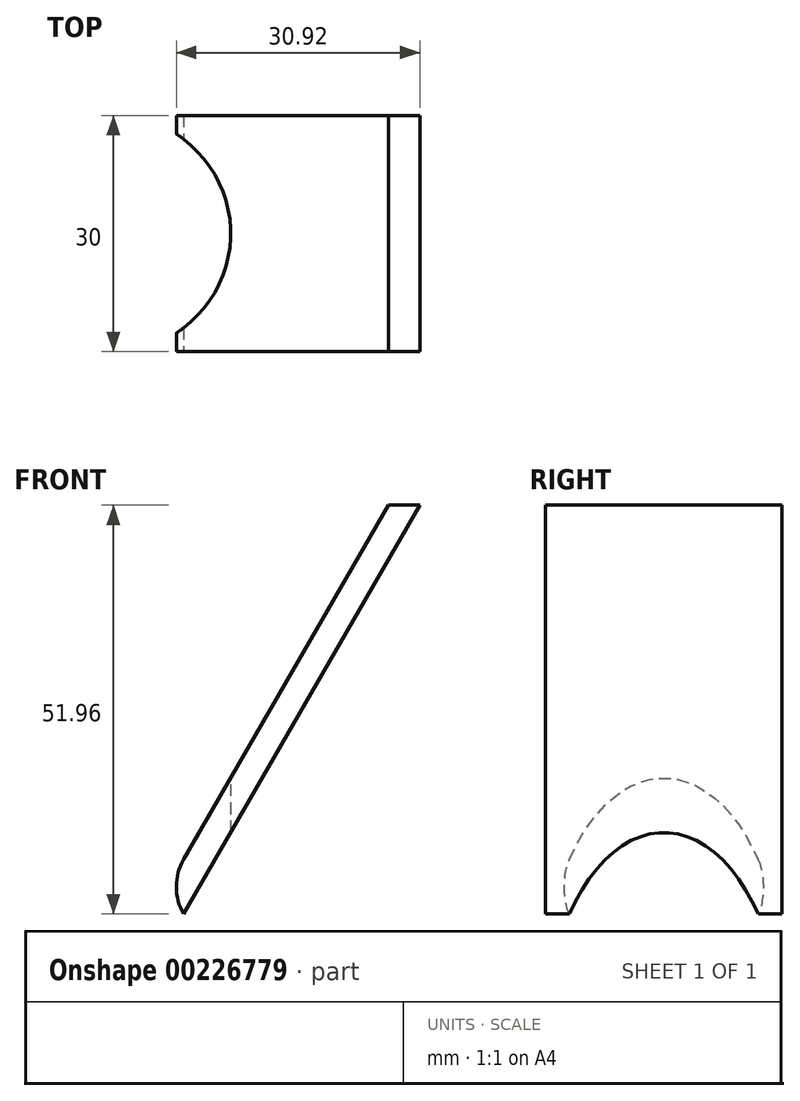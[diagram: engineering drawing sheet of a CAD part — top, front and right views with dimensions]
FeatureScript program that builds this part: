
annotation { "Feature Type Name" : "Feature", "Feature Type Description" : "" }
export const myFeature = defineFeature(function(context is Context, id is Id, definition is map)
    precondition{}
    {
        {
            var Q0;
            Q0=qCreatedBy(makeId("Top.planeOp"),FACE);
            var sketch = newSketch(context, id + "F0", { "sketchPlane" : qUnion([Q0])});
            skCircle(sketch, "E0", {"center": v(0, 0) * mm, "radius": 15 * mm});
            skCircle(sketch, "E1", {"center": v(0, 0) * mm, "radius": 12 * mm});
            skCircle(sketch, "E2", {"center": v(0, 0) * mm, "radius": 1.75 * mm});
            skSolve(sketch);
        }
        {
            var Q0;
            Q0=makeQuery(id+"F0.imprint","IMPRINT",FACE,{"disambiguationData":[TD([[makeQuery(id+"F0.imprint","IMPRINT",EDGE,{"derivedFrom":sQuery(id+"F0.wireOp",EDGE,"E0")}),1.0]])]});
            extrude(context, id + "F1", {"entities" : qUnion([Q0]), "oppositeDirection" : true, "depth" : 90 * mm});
        }
        {
            var Q0;
            Q0=makeQuery(id+"F0.imprint","IMPRINT",FACE,{"disambiguationData":[TD([[makeQuery(id+"F0.imprint","IMPRINT",EDGE,{"derivedFrom":sQuery(id+"F0.wireOp",EDGE,"E1")}),1.0]])]});
            extrude(context, id + "F2", {"entities" : qUnion([Q0]), "operationType" : NewBodyOperationType.ADD, "oppositeDirection" : true, "depth" : 8 * mm});
        }
        {
            var Q0;
            Q0=qCreatedBy(makeId("Right.planeOp"),FACE);
            cPlane(context, id + "F3", {"entities" : qUnion([Q0]), "cplaneType" : CPlaneType.OFFSET, "offset" : 15 * mm, "width" : 150 * mm, "height" : 150 * mm});
        }
        {
            var Q0;
            Q0=qCreatedBy(id+"F3.planeOp",FACE);
            var sketch = newSketch(context, id + "F4", { "sketchPlane" : qUnion([Q0])});
            skCircle(sketch, "E3", {"center": v(0, -25.75) * mm, "radius": 14.75 * mm});
            skLineSegment(sketch, "E4", {"start": v(12.69, -18.23) * mm, "end": v(12.69, -33.27) * mm});
            skLineSegment(sketch, "E5", {"start": v(-12.69, -18.23) * mm, "end": v(-12.69, -33.27) * mm});
            skLineSegment(sketch, "E6", {"start": v(-12.69, -18.23) * mm, "end": v(12.69, -18.23) * mm, "construction": true});
            skLineSegment(sketch, "E7", {"start": v(-12.69, -33.27) * mm, "end": v(12.69, -33.27) * mm, "construction": true});
            skLineSegment(sketch, "E8", {"start": v(-12.69, -25.75) * mm, "end": v(12.69, -25.75) * mm, "construction": true});
            skSolve(sketch);
        }
        {
            var Q0;
            {var subQ0=sQuery(id+"F4.wireOp",EDGE,"E4");Q0=makeQuery(id+"F4.imprint","IMPRINT",FACE,{"disambiguationData":[TD([[makeQuery(id+"F4.imprint","IMPRINT",EDGE,{"derivedFrom":subQ0}),-1.0]])]});}
            extrude(context, id + "F5", {"entities" : qUnion([Q0]), "operationType" : NewBodyOperationType.REMOVE, "oppositeDirection" : true, "depth" : 11.6 * mm});
        }
        {
            var Q0;
            Q0=makeQuery(id+"F5.boolean.opBoolean","INTERSECT",EDGE,{"disambiguationData":[OD(1.0)],"derivedFrom":[makeQuery(id+"F1.opExtrude","SWEPT_FACE",FACE,{"disambiguationData":[OSD([sQuery(id+"F0.wireOp",EDGE,"E1")])]}),makeQuery(id+"F5.opExtrude","CAP_FACE",FACE,{"disambiguationData":[OSD([sQuery(id+"F4.wireOp",EDGE,"E3"),sQuery(id+"F4.wireOp",EDGE,"E4"),sQuery(id+"F4.wireOp",EDGE,"E5")])],"isStart":false})]});
            var Q1;
            Q1=makeQuery(id+"F5.boolean.opBoolean","INTERSECT",EDGE,{"disambiguationData":[OD(0.0)],"derivedFrom":[makeQuery(id+"F1.opExtrude","SWEPT_FACE",FACE,{"disambiguationData":[OSD([sQuery(id+"F0.wireOp",EDGE,"E1")])]}),makeQuery(id+"F5.opExtrude","CAP_FACE",FACE,{"disambiguationData":[OSD([sQuery(id+"F4.wireOp",EDGE,"E3"),sQuery(id+"F4.wireOp",EDGE,"E4"),sQuery(id+"F4.wireOp",EDGE,"E5")])],"isStart":false})]});
            fillet(context, id + "F6", {"entities" : qUnion([Q0, Q1]), "radius" : 5 * mm, "tangentPropagation" : true, "allowEdgeOverflow" : false});
        }
        {
            var Q0;
            Q0=qCreatedBy(makeId("Front.planeOp"),FACE);
            cPlane(context, id + "F7", {"entities" : qUnion([Q0]), "cplaneType" : CPlaneType.OFFSET, "offset" : 15 * mm, "width" : 150 * mm, "height" : 150 * mm});
        }
        {
            var Q0;
            Q0=qCreatedBy(id+"F7.planeOp",FACE);
            var sketch = newSketch(context, id + "F8", { "sketchPlane" : qUnion([Q0])});
            skLineSegment(sketch, "E9.bottom", {"start": v(39, -28) * mm, "end": v(35, -28) * mm});
            skLineSegment(sketch, "E9.top", {"start": v(9, -79.96) * mm, "end": v(5, -79.96) * mm});
            skLineSegment(sketch, "E9.left", {"start": v(39, -28) * mm, "end": v(9, -79.96) * mm});
            skLineSegment(sketch, "E9.right", {"start": v(35, -28) * mm, "end": v(5, -79.96) * mm});
            skLineSegment(sketch, "E10", {"start": v(64.63, 0) * mm, "end": v(-54.1, 0) * mm});
            skSolve(sketch);
        }
        {
            var Q0;
            Q0=makeQuery(id+"F8.imprint","IMPRINT",FACE,{"disambiguationData":[TD([[makeQuery(id+"F8.imprint","IMPRINT",EDGE,{"derivedFrom":sQuery(id+"F8.wireOp",EDGE,"E9.bottom")}),1.0]])]});
            extrude(context, id + "F9", {"entities" : qUnion([Q0]), "oppositeDirection" : true, "depth" : 30 * mm});
        }
        {
            var Q0;
            Q0=makeQuery(id+"F9.opExtrude","SWEPT_EDGE",EDGE,{"disambiguationData":[OSD([sQuery(id+"F8.wireOp",EDGE,"E9.top"),sQuery(id+"F8.wireOp",EDGE,"E9.right")])]});
            fillet(context, id + "F10", {"entities" : qUnion([Q0]), "radius" : 7 * mm, "tangentPropagation" : true, "allowEdgeOverflow" : false});
        }
        {
            var Q0;
            Q0=makeQuery(id+"F0.imprint","IMPRINT",FACE,{"disambiguationData":[TD([[makeQuery(id+"F0.imprint","IMPRINT",EDGE,{"derivedFrom":sQuery(id+"F0.wireOp",EDGE,"E1")}),1.0]])]});
            var Q1;
            Q1=makeQuery(id+"F0.imprint","IMPRINT",FACE,{"disambiguationData":[TD([[makeQuery(id+"F0.imprint","IMPRINT",EDGE,{"derivedFrom":sQuery(id+"F0.wireOp",EDGE,"E0")}),1.0]])]});
            extrude(context, id + "F11", {"entities" : qUnion([Q0, Q1]), "operationType" : NewBodyOperationType.REMOVE, "oppositeDirection" : true, "depth" : 103.2 * mm});
        }
    });
